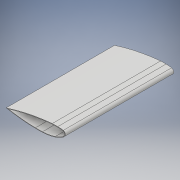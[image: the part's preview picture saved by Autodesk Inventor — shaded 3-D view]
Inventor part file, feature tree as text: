
AUTODESK INVENTOR PART (.ipt)
format: ipt  version: 2018 (Build 220112000, 112)  size: 133,632 bytes
history: native  units: mm
features: extrude x1, shell x1, sketch x1, projected_geometry x1
ambient origin geometry x8: Origin, YZ Plane, XZ Plane, XY Plane, X Axis, Y Axis, Z Axis, Center Point
bodies: Body1 (feature_tree)
feature tree (4):
  extrude  "押し出し1"  Depth=394.0mm TaperAngle=0.0deg
  shell  "シェル1"  Thickness=2.0mm
  sketch  "スケッチ1"
  projected_geometry  "投影ループ1"
